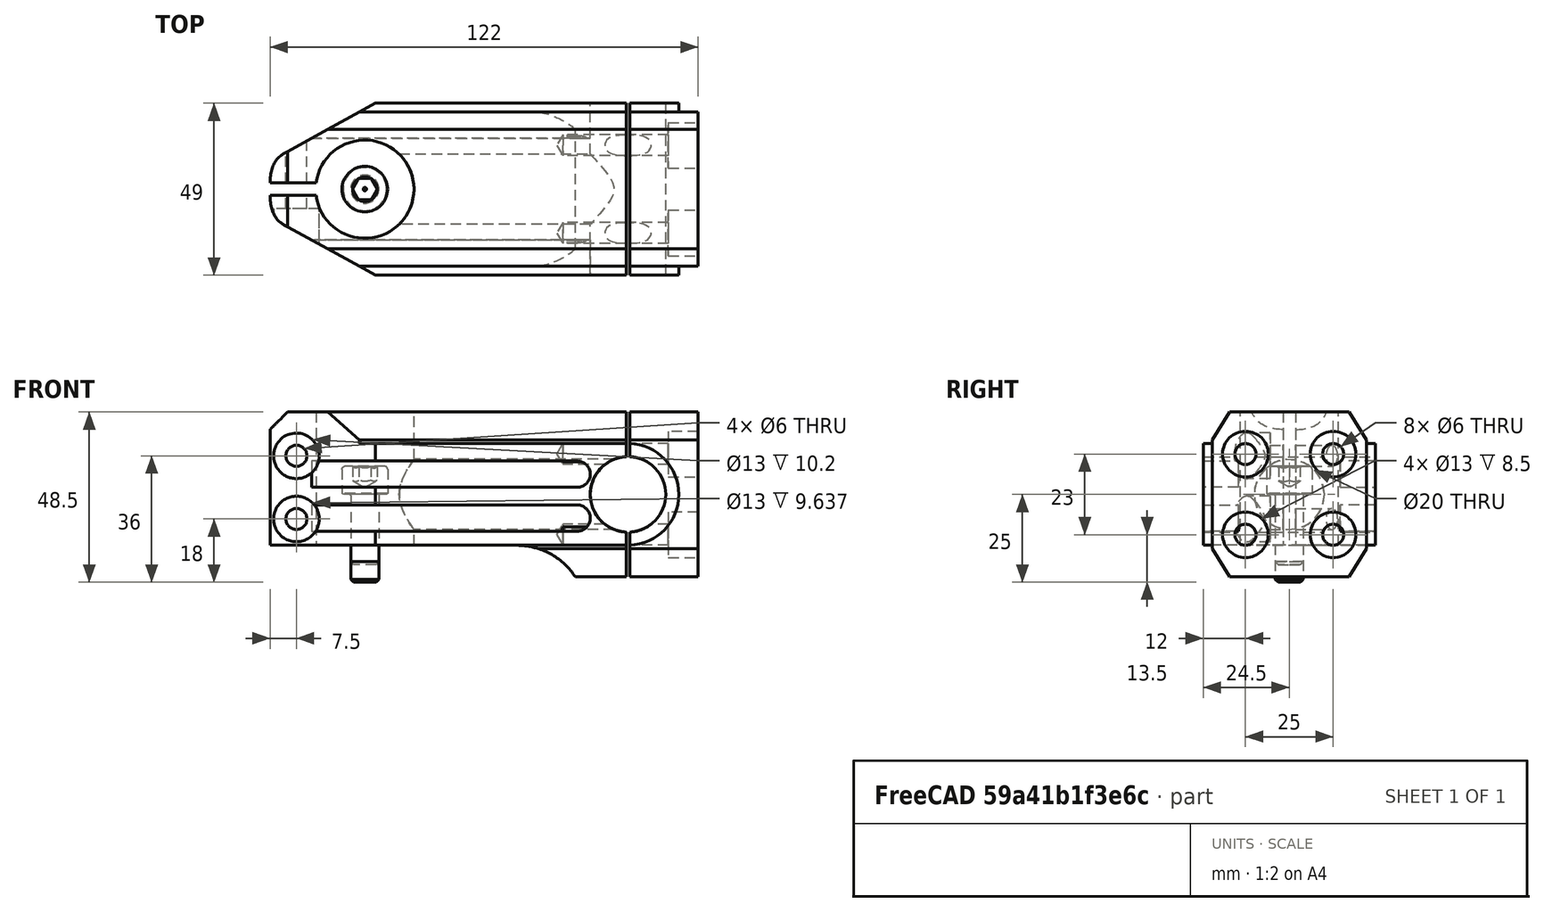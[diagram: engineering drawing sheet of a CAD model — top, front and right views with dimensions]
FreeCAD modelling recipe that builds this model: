
FCSTD DOCUMENT  (FreeCAD 1.0R39109 (Git))
Label: Anchor
License: All rights reserved
LicenseURL: https://en.wikipedia.org/wiki/All_rights_reserved
objects: Sketcher::SketchObject×11, PartDesign::Pocket×9, App::Link×7, App::FeaturePython×7, PartDesign::Pad×2, PartDesign::Hole×2, Part::FeaturePython×2, App::VarSet×1, PartDesign::Chamfer×1, PartDesign::Mirrored×1, PartDesign::Body×1, App::Part×1, Assembly::JointGroup×1, Assembly::AssemblyObject×1
note: 69 computed .brp shape members not serialized (recipe doc carries the construction recipe); baked Part::Feature solids carry a one-line shape summary decoded from their .brp

FEATURE [Sketcher::SketchObject] Sketch
  ArcFitTolerance = 1e-06
  AttachmentSupport = -> [XZ_Plane001]
  FullyConstrained = true
  MakeInternals = false
  MapMode = 5
  Placement = pos=(0,0,0) rot=(1,0,0;1.5708rad)
  expr: Constraints[15] = <<VarSet>>.Size
  expr: Constraints[16] = <<VarSet>>.Size + 20 mm
  sketch-geometry (7):
    g0: Circle CenterX=75 CenterY=0 CenterZ=0 NormalX=0 NormalY=0 NormalZ=1 AngleXU=0 Radius=10.75
    g1: LineSegment StartX=0 StartY=23.5 StartZ=0 EndX=95 EndY=23.5 EndZ=0
    g2: LineSegment StartX=95 StartY=23.5 StartZ=0 EndX=95 EndY=-23.5 EndZ=0
    g3: LineSegment StartX=95 StartY=-23.5 StartZ=0 EndX=0 EndY=-23.5 EndZ=0
    g4: LineSegment StartX=0 StartY=-23.5 StartZ=0 EndX=-27 EndY=-23.5 EndZ=0
    g5: LineSegment StartX=-27 StartY=-23.5 StartZ=0 EndX=-27 EndY=23.5 EndZ=0
    g6: LineSegment StartX=-27 StartY=23.5 StartZ=0 EndX=0 EndY=23.5 EndZ=0
  constraints (20):
    c: Diameter(g0) = 21.5
    c: PointOnObject(g0,g-1)
    c: PointOnObject(g1,g-2)
    c: Horizontal(g1)
    c: Coincident(g1,g2)
    c: Coincident(g2,g3)
    c: PointOnObject(g3,g-2)
    c: Horizontal(g3)
    c: Coincident(g3,g4)
    c: Horizontal(g4)
    c: Coincident(g4,g5)
    c: Vertical(g5)
    c: Coincident(g5,g6)
    c: Coincident(g6,g1)
    c: Parallel(g6,g-1)
    c: Distance(g0,g-1) = 75
    c: Distance(g1) = 95
    c: Distance(g2) = 47
    c: Distance(g4) = 27
    c: Symmetric(g1,g2,g-1)
FEATURE [App::VarSet] VarSet
  Size = 75
FEATURE [PartDesign::Pad] Pad
  Direction = (0,-1,2e-16)
  Length = 22
  Length2 = 10
  Placement = pos=(0,0,0) rot=(1,0,0;1.5708rad)
  Profile = -> Sketch
  ReferenceAxis = -> Sketch [N_Axis]
  Refine = true
  Suppressed = false
  Type = 0
FEATURE [PartDesign::Chamfer] Chamfer
  Angle = 45
  Base = -> Pad [Edge14,Edge15]
  BaseFeature = -> Pad
  ChamferType = 1
  FlipDirection = false
  Placement = pos=(0,0,0) rot=(1,0,0;1.5708rad)
  Refine = true
  Size = 8
  Size2 = 5
  SupportTransform = false
  Suppressed = false
  UseAllEdges = false
FEATURE [Sketcher::SketchObject] Sketch001
  ArcFitTolerance = 1e-06
  AttachmentSupport = -> [Chamfer]
  ExternalGeometry = -> [Chamfer]
  FullyConstrained = true
  MakeInternals = false
  MapMode = 5
  Placement = pos=(0,-22,0) rot=(1,0,0;1.5708rad)
  sketch-geometry (5):
    g0: ArcOfCircle CenterX=75 CenterY=4.9e-15 CenterZ=0 NormalX=0 NormalY=0 NormalZ=1 AngleXU=0 Radius=14.5 StartAngle=4.71239 EndAngle=7.85398
    g1: LineSegment StartX=75 StartY=14.5 StartZ=0 EndX=-27 EndY=14.5 EndZ=0
    g2: LineSegment StartX=75 StartY=-14.5 StartZ=0 EndX=-27 EndY=-14.5 EndZ=0
    g3: LineSegment StartX=-27 StartY=14.5 StartZ=0 EndX=-27 EndY=-14.5 EndZ=0
    g4: Circle CenterX=75 CenterY=4.9e-15 CenterZ=0 NormalX=0 NormalY=0 NormalZ=1 AngleXU=0 Radius=10.75
  constraints (14):
    c: Coincident(g0,g-4)
    c: Vertical(g0,g0)
    c: Vertical(g0,g0)
    c: Coincident(g0,g1)
    c: Coincident(g0,g2)
    c: Horizontal(g1)
    c: Horizontal(g2)
    c: Radius(g0) = 14.5
    c: Vertical(g3)
    c: Coincident(g1,g3)
    c: Coincident(g2,g3)
    c: Distance(g-1,g3) = 27
    c: Coincident(g4,g0)
    c: Equal(g4,g-4)
FEATURE [PartDesign::Pad] Pad001
  BaseFeature = -> Chamfer
  Direction = (0,-1,2e-16)
  Length = 2.5
  Length2 = 10
  Placement = pos=(0,0,0) rot=(1,0,0;1.5708rad)
  Profile = -> Sketch001
  ReferenceAxis = -> Sketch001 [N_Axis]
  Refine = true
  Suppressed = false
  Type = 0
FEATURE [Sketcher::SketchObject] Sketch002
  ArcFitTolerance = 1e-06
  AttachmentSupport = -> [Pad001]
  ExternalGeometry = -> [Pad001]
  FullyConstrained = true
  MakeInternals = false
  MapMode = 5
  Placement = pos=(0,-24.5,6.1e-15) rot=(1,0,0;1.5708rad)
  expr: Constraints[18] = VarSet.Size - 14.5 mm
  sketch-geometry (8):
    g0: LineSegment StartX=-27 StartY=9.5 StartZ=0 EndX=-27 EndY=2 EndZ=0
    g1: LineSegment StartX=-27 StartY=2 StartZ=0 EndX=60.5 EndY=2 EndZ=0
    g2: LineSegment StartX=60.5 StartY=9.5 StartZ=0 EndX=-27 EndY=9.5 EndZ=0
    g3: LineSegment StartX=-27 StartY=-3 StartZ=0 EndX=-27 EndY=-10.5 EndZ=0
    g4: LineSegment StartX=-27 StartY=-10.5 StartZ=0 EndX=60.5 EndY=-10.5 EndZ=0
    g5: LineSegment StartX=60.5 StartY=-3 StartZ=0 EndX=-27 EndY=-3 EndZ=0
    g6: ArcOfCircle CenterX=60.5 CenterY=5.75 CenterZ=0 NormalX=0 NormalY=0 NormalZ=1 AngleXU=0 Radius=3.75 StartAngle=4.71239 EndAngle=7.85398
    g7: ArcOfCircle CenterX=60.5 CenterY=-6.75 CenterZ=0 NormalX=0 NormalY=0 NormalZ=1 AngleXU=0 Radius=3.75 StartAngle=4.71239 EndAngle=7.85398
  constraints (22):
    c: Coincident(g0,g1)
    c: Coincident(g2,g0)
    c: Vertical(g0)
    c: Horizontal(g1)
    c: Horizontal(g2)
    c: PointOnObject(g0,g-3)
    c: Coincident(g3,g4)
    c: Coincident(g5,g3)
    c: Vertical(g3)
    c: Horizontal(g4)
    c: Horizontal(g5)
    c: PointOnObject(g3,g-3)
    c: Tangent(g6,g2) = -1.5708
    c: Tangent(g6,g1) = -1.5708
    c: Tangent(g7,g5) = -1.5708
    c: Tangent(g7,g4) = -1.5708
    c: Distance(g1,g2) = 7.5
    c: Distance(g-1,g1) = 2
    c: Distance(g6,g-2) = 60.5
    c: Vertical(g6,g7)
    c: Equal(g3,g0)
    c: Distance(g-1,g5) = 3
FEATURE [PartDesign::Pocket] Pocket
  BaseFeature = -> Pad001
  Direction = (0,1,-2e-16)
  Length = 10
  Length2 = 5
  Placement = pos=(0,0,0) rot=(1,0,0;1.5708rad)
  Profile = -> Sketch002
  ReferenceAxis = -> Sketch002 [N_Axis]
  Refine = true
  Suppressed = false
  Type = 0
FEATURE [Sketcher::SketchObject] Sketch003
  ArcFitTolerance = 1e-06
  AttachmentSupport = -> [Pocket]
  ExternalGeometry = -> [Pocket]
  FullyConstrained = true
  MakeInternals = false
  MapMode = 5
  Placement = pos=(0,-22,0) rot=(1,0,0;1.5708rad)
  expr: Constraints[9] = VarSet.Size - 15 mm
  sketch-geometry (5):
    g0: LineSegment StartX=43.2967 StartY=-14.5 StartZ=0 EndX=-27 EndY=-14.5 EndZ=0
    g1: LineSegment StartX=-27 StartY=-14.5 StartZ=0 EndX=-27 EndY=-23.5 EndZ=0
    g2: LineSegment StartX=-27 StartY=-23.5 StartZ=0 EndX=0 EndY=-23.5 EndZ=0
    g3: LineSegment StartX=0 StartY=-23.5 StartZ=0 EndX=60 EndY=-23.5 EndZ=0
    g4: ArcOfCircle CenterX=43.2967 CenterY=-34.5 CenterZ=0 NormalX=0 NormalY=0 NormalZ=1 AngleXU=0 Radius=20 StartAngle=0.582364 EndAngle=1.5708
  constraints (13):
    c: PointOnObject(g0,g-5)
    c: Coincident(g0,g-5)
    c: Coincident(g0,g1)
    c: Coincident(g1,g-4)
    c: Coincident(g1,g2)
    c: PointOnObject(g2,g-3)
    c: Coincident(g2,g3)
    c: PointOnObject(g3,g-3)
    c: PointOnObject(g2,g-2)
    c: DistanceX(g3,g3) = 60
    c: Coincident(g3,g4)
    c: Tangent(g4,g0) = -1.5708
    c: Radius(g4) = 20
FEATURE [PartDesign::Pocket] Pocket001
  BaseFeature = -> Pocket
  Direction = (0,1,-2e-16)
  Length = 5
  Length2 = 5
  Placement = pos=(0,0,0) rot=(1,0,0;1.5708rad)
  Profile = -> Sketch003
  ReferenceAxis = -> Sketch003 [N_Axis]
  Refine = true
  Suppressed = false
  Type = 1
FEATURE [Sketcher::SketchObject] Sketch004
  ArcFitTolerance = 1e-06
  AttachmentSupport = -> [Pocket001]
  ExternalGeometry = -> [Pocket001]
  FullyConstrained = true
  MakeInternals = false
  MapMode = 5
  Placement = pos=(0,1.13e-14,23.5) rot=(0,0,1;3.14159rad)
  sketch-geometry (10):
    g0: LineSegment StartX=-3 StartY=24.5 StartZ=0 EndX=27 EndY=24.5 EndZ=0
    g1: LineSegment StartX=27 StartY=24.5 StartZ=0 EndX=27 EndY=1.75 EndZ=0
    g2: LineSegment StartX=-3 StartY=24.5 StartZ=0 EndX=23 EndY=10.2 EndZ=0
    g3: LineSegment [constr] StartX=23 StartY=10.2 StartZ=0 EndX=27 EndY=8 EndZ=0
    g4: Circle [constr] CenterX=23 CenterY=10.2 CenterZ=0 NormalX=0 NormalY=0 NormalZ=1 AngleXU=0 Radius=1
    g5: Circle [constr] CenterX=27 CenterY=8 CenterZ=0 NormalX=0 NormalY=0 NormalZ=1 AngleXU=0 Radius=1
    g6: Circle [constr] CenterX=27 CenterY=1.75 CenterZ=0 NormalX=0 NormalY=0 NormalZ=1 AngleXU=0 Radius=1
    g7: BSplineCurve PolesCount=3 KnotsCount=2 Degree=2 IsPeriodic=0
    g8: GeomPoint [constr] X=23 Y=10.2 Z=0
    g9: GeomPoint [constr] X=27 Y=1.75 Z=0
  constraints (23):
    c: PointOnObject(g0,g-3)
    c: Coincident(g0,g-4)
    c: Coincident(g0,g1)
    c: PointOnObject(g1,g-6)
    c: DistanceY(g-6,g1) = 1.75
    c: Distance(g0,g-2) = 3
    c: Coincident(g0,g2)
    c: Distance(g2,g-2) = 23
    c: Coincident(g3,g2)
    c: PointOnObject(g3,g1)
    c: Parallel(g3,g2)
    c: DistanceY(g-6,g3) = 8
    c: Weight(g4) = 1
    c: Equal(g4,g5)
    c: Equal(g4,g6)
    c: InternalAlignment(g4,g7)
    c: InternalAlignment(g5,g7)
    c: InternalAlignment(g6,g7)
    c: InternalAlignment(g8,g7)
    c: InternalAlignment(g9,g7)
    c: Coincident(g4,g2)
    c: Coincident(g6,g1)
    c: Coincident(g5,g3)
FEATURE [PartDesign::Pocket] Pocket002
  BaseFeature = -> Pocket001
  Direction = (0,0,-1)
  Length = 5
  Length2 = 5
  Placement = pos=(0,0,0) rot=(1,0,0;1.5708rad)
  Profile = -> Sketch004
  ReferenceAxis = -> Sketch004 [N_Axis]
  Refine = true
  Suppressed = false
  Type = 1
FEATURE [PartDesign::Mirrored] Mirrored
  BaseFeature = -> Pocket002
  MirrorPlane = -> XZ_Plane001
  Placement = pos=(0,0,0) rot=(1,0,0;1.5708rad)
  Refine = true
  Suppressed = false
  TransformMode = 1
FEATURE [Sketcher::SketchObject] Sketch005
  ArcFitTolerance = 1e-06
  AttachmentSupport = -> [Mirrored]
  ExternalGeometry = -> [Mirrored]
  FullyConstrained = true
  MakeInternals = false
  MapMode = 5
  Placement = pos=(0,0,23.5) rot=(0,0,1;3.14159rad)
  sketch-geometry (4):
    g0: ArcOfCircle CenterX=0 CenterY=0 CenterZ=0 NormalX=0 NormalY=0 NormalZ=1 AngleXU=0 Radius=14 StartAngle=0.125328 EndAngle=6.15786
    g1: LineSegment StartX=27 StartY=1.75 StartZ=0 EndX=13.8902 EndY=1.75 EndZ=0
    g2: LineSegment StartX=27 StartY=-1.75 StartZ=0 EndX=13.8902 EndY=-1.75 EndZ=0
    g3: LineSegment StartX=27 StartY=1.75 StartZ=0 EndX=27 EndY=-1.75 EndZ=0
  constraints (10):
    c: Diameter(g0) = 28
    c: Coincident(g0,g-1)
    c: Coincident(g1,g-3)
    c: Horizontal(g1)
    c: Coincident(g2,g-3)
    c: Horizontal(g2)
    c: Coincident(g3,g1)
    c: Coincident(g3,g2)
    c: Coincident(g0,g2)
    c: Coincident(g0,g1)
FEATURE [PartDesign::Pocket] Pocket003
  BaseFeature = -> Mirrored
  Direction = (0,0,-1)
  Length = 5
  Length2 = 5
  Placement = pos=(0,0,0) rot=(1,0,0;1.5708rad)
  Profile = -> Sketch005
  ReferenceAxis = -> Sketch005 [N_Axis]
  Refine = true
  Suppressed = false
  Type = 1
FEATURE [Sketcher::SketchObject] Sketch006
  ArcFitTolerance = 1e-06
  AttachmentSupport = -> [XZ_Plane001]
  ExternalGeometry = -> [Pocket003]
  FullyConstrained = true
  MakeInternals = false
  MapMode = 5
  Placement = pos=(0,0,0) rot=(1,0,0;1.5708rad)
  sketch-geometry (3):
    g0: LineSegment StartX=-27 StartY=23.5 StartZ=0 EndX=-22 EndY=23.5 EndZ=0
    g1: LineSegment StartX=-22 StartY=23.5 StartZ=0 EndX=-27 EndY=18.5 EndZ=0
    g2: LineSegment StartX=-27 StartY=18.5 StartZ=0 EndX=-27 EndY=23.5 EndZ=0
  constraints (8):
    c: Coincident(g0,g-4)
    c: PointOnObject(g0,g-5)
    c: Coincident(g0,g1)
    c: PointOnObject(g1,g-3)
    c: Coincident(g1,g2)
    c: Coincident(g2,g0)
    c: DistanceX(g0,g0) = 5
    c: DistanceY(g2,g2) = 5
FEATURE [PartDesign::Pocket] Pocket004
  BaseFeature = -> Pocket003
  Direction = (0,1,-2e-16)
  Length = 5
  Length2 = 5
  Midplane = true
  Placement = pos=(0,0,0) rot=(1,0,0;1.5708rad)
  Profile = -> Sketch006
  ReferenceAxis = -> Sketch006 [N_Axis]
  Refine = true
  Suppressed = false
  Type = 1
FEATURE [Sketcher::SketchObject] Sketch007
  ArcFitTolerance = 1e-06
  AttachmentSupport = -> [Pocket004]
  FullyConstrained = true
  MakeInternals = false
  MapMode = 5
  Placement = pos=(95,0,0) rot=(0.707107,0,0.707107;3.14159rad)
  sketch-geometry (4):
    g0: Circle CenterX=11.5 CenterY=12.5 CenterZ=0 NormalX=0 NormalY=0 NormalZ=1 AngleXU=0 Radius=6.5
    g1: Circle CenterX=-11.5 CenterY=12.5 CenterZ=0 NormalX=0 NormalY=0 NormalZ=1 AngleXU=0 Radius=6.5
    g2: Circle CenterX=-11.5 CenterY=-12.5 CenterZ=0 NormalX=0 NormalY=0 NormalZ=1 AngleXU=0 Radius=6.5
    g3: Circle CenterX=11.5 CenterY=-12.5 CenterZ=0 NormalX=0 NormalY=0 NormalZ=1 AngleXU=0 Radius=6.5
  constraints (9):
    c: Symmetric(g0,g3,g-1)
    c: Symmetric(g1,g2,g-1)
    c: Symmetric(g2,g3,g-2)
    c: DistanceX(g1,g0) = 23
    c: DistanceY(g3,g0) = 25
    c: Equal(g0,g1)
    c: Equal(g1,g2)
    c: Equal(g2,g3)
    c: Diameter(g0) = 13
FEATURE [PartDesign::Pocket] Pocket005
  BaseFeature = -> Pocket004
  Direction = (-1,0,2e-16)
  Length = 8.5
  Length2 = 5
  Placement = pos=(0,0,0) rot=(1,0,0;1.5708rad)
  Profile = -> Sketch007
  ReferenceAxis = -> Sketch007 [N_Axis]
  Refine = true
  Suppressed = false
  Type = 0
FEATURE [PartDesign::Hole] Hole
  BaseFeature = -> Pocket005
  CustomThreadClearance = 0
  Depth = 30
  DepthType = 0
  Diameter = 6
  DrillForDepth = false
  DrillPoint = 1
  DrillPointAngle = 118
  HoleCutCountersinkAngle = 90
  HoleCutCustomValues = false
  HoleCutDepth = 0
  HoleCutDiameter = 6.1
  HoleCutType = 0
  ModelThread = false
  Placement = pos=(0,0,0) rot=(1,0,0;1.5708rad)
  Profile = -> Pocket005 [Face49,Face47,Face46,Face48]
  Refine = true
  Suppressed = false
  Tapered = false
  TaperedAngle = 90
  ThreadClass = 0
  ThreadDepth = 30
  ThreadDepthType = 0
  ThreadDirection = 0
  ThreadFit = 0
  ThreadSize = 0
  ThreadType = 0
  Threaded = false
  UseCustomThreadClearance = false
FEATURE [Sketcher::SketchObject] Sketch008
  ArcFitTolerance = 1e-06
  AttachmentSupport = -> [Hole]
  FullyConstrained = true
  MakeInternals = false
  MapMode = 5
  Placement = pos=(0,-14.5,4.8e-15) rot=(1,0,0;1.5708rad)
  sketch-geometry (2):
    g0: Circle CenterX=-19.5 CenterY=11 CenterZ=0 NormalX=0 NormalY=0 NormalZ=1 AngleXU=0 Radius=6.5
    g1: Circle CenterX=-19.5 CenterY=-7 CenterZ=0 NormalX=0 NormalY=0 NormalZ=1 AngleXU=0 Radius=6.5
  constraints (6):
    c: Vertical(g0,g1)
    c: Equal(g1,g0)
    c: DistanceY(g1,g-1) = 7
    c: Distance(g0,g-1) = 11
    c: DistanceX(g0,g-1) = 19.5
    c: Diameter(g0) = 13
FEATURE [PartDesign::Pocket] Pocket006
  BaseFeature = -> Hole
  Direction = (0,1,-2e-16)
  Length = 9
  Length2 = 7
  Placement = pos=(0,0,0) rot=(1,0,0;1.5708rad)
  Profile = -> Sketch008
  ReferenceAxis = -> Sketch008 [N_Axis]
  Refine = true
  Suppressed = false
  Type = 4
FEATURE [PartDesign::Hole] Hole001
  BaseFeature = -> Pocket006
  CustomThreadClearance = 0
  Depth = 25
  DepthType = 0
  Diameter = 6
  DrillForDepth = false
  DrillPoint = 1
  DrillPointAngle = 118
  HoleCutCountersinkAngle = 90
  HoleCutCustomValues = false
  HoleCutDepth = 0
  HoleCutDiameter = 6.1
  HoleCutType = 0
  ModelThread = false
  Placement = pos=(0,0,0) rot=(1,0,0;1.5708rad)
  Profile = -> Pocket006 [Face33,Face57]
  Refine = true
  Suppressed = false
  Tapered = false
  TaperedAngle = 90
  ThreadClass = 0
  ThreadDepth = 25
  ThreadDepthType = 0
  ThreadDirection = 0
  ThreadFit = 0
  ThreadSize = 0
  ThreadType = 0
  Threaded = false
  UseCustomThreadClearance = false
FEATURE [Sketcher::SketchObject] Sketch009
  ArcFitTolerance = 1e-06
  AttachmentSupport = -> [XZ_Plane001]
  ExternalGeometry = -> [Hole001]
  FullyConstrained = true
  MakeInternals = false
  MapMode = 5
  Placement = pos=(0,0,0) rot=(1,0,0;1.5708rad)
  expr: Constraints[10] = VarSet.Size + 0.5 mm
  expr: Constraints[9] = VarSet.Size - 0.5 mm
  sketch-geometry (4):
    g0: LineSegment StartX=74.5 StartY=23.5 StartZ=0 EndX=74.5 EndY=-23.5 EndZ=0
    g1: LineSegment StartX=74.5 StartY=-23.5 StartZ=0 EndX=75.5 EndY=-23.5 EndZ=0
    g2: LineSegment StartX=75.5 StartY=-23.5 StartZ=0 EndX=75.5 EndY=23.5 EndZ=0
    g3: LineSegment StartX=75.5 StartY=23.5 StartZ=0 EndX=74.5 EndY=23.5 EndZ=0
  constraints (12):
    c: Coincident(g0,g1)
    c: Coincident(g1,g2)
    c: Coincident(g2,g3)
    c: Coincident(g3,g0)
    c: Vertical(g0)
    c: Vertical(g2)
    c: Horizontal(g1)
    c: Horizontal(g3)
    c: PointOnObject(g0,g-3)
    c: Distance(g-2,g0) = 74.5
    c: Distance(g-2,g2) = 75.5
    c: PointOnObject(g0,g-4)
FEATURE [PartDesign::Pocket] Pocket007
  BaseFeature = -> Hole001
  Direction = (0,1,-2e-16)
  Length = 5
  Length2 = 5
  Midplane = true
  Placement = pos=(0,0,0) rot=(1,0,0;1.5708rad)
  Profile = -> Sketch009
  ReferenceAxis = -> Sketch009 [N_Axis]
  Refine = true
  Suppressed = false
  Type = 1
FEATURE [Sketcher::SketchObject] Sketch010
  ArcFitTolerance = 1e-06
  AttachmentSupport = -> [YZ_Plane001]
  FullyConstrained = true
  MakeInternals = false
  MapMode = 5
  Placement = pos=(0,0,0) rot=(0.57735,0.57735,0.57735;2.0944rad)
  sketch-geometry (1):
    g0: Circle CenterX=0 CenterY=0 CenterZ=0 NormalX=0 NormalY=0 NormalZ=1 AngleXU=0 Radius=10
  constraints (2):
    c: Diameter(g0) = 20
    c: Coincident(g0,g-1)
FEATURE [PartDesign::Pocket] Pocket008
  BaseFeature = -> Pocket007
  Direction = (-1,0,0)
  Length = 0
  Length2 = 5
  Placement = pos=(0,0,0) rot=(1,0,0;1.5708rad)
  Profile = -> Sketch010
  ReferenceAxis = -> Sketch010 [N_Axis]
  Refine = true
  Suppressed = false
  Type = 3
  UpToFace = -> Pocket007 [Face18]
FEATURE [PartDesign::Body] Body  label="Stem"
  AllowCompound = true
  Group = -> [Sketch,Pad,Chamfer,Sketch001,Pad001,Sketch002,Pocket,Sketch003,Pocket001,Sketch004,Pocket002,Mirrored,Sketch005,Pocket003,Sketch006,Pocket004,Sketch007,Pocket005,Hole,Sketch008,Pocket006,Hole001,Sketch009,Pocket007,Sketch010,Pocket008]
  Origin = -> Origin001
  Tip = -> Pocket008
FEATURE [App::Part] Part
  Group = -> [Body,VarSet]
  Origin = -> Origin
FEATURE [Part::FeaturePython] Screw  label="M8x25-Screw"  # WARN: FeaturePython — macro-defined, semantics opaque (R4)
  Diameter = 8
  Invert = false
  LeftHanded = false
  Length = 5
  LengthCustom = 25
  MatchOuter = false
  OffsetAngle = 0
  Thread = false
  Type = 75
FEATURE [App::Link] Stem  label="Stem001"
  LinkedObject = -> Body
FEATURE [App::FeaturePython] GroundedJoint  # Assembly grounded joint (typed FeaturePython)
  ObjectToGround = -> Stem
FEATURE [App::Link] M8x25_Screw  label="M8x25-Screw001"
  LinkPlacement = pos=(87.5,-12.5,-11.5) rot=(0.707107,0,0.707107;3.14159rad)
  LinkedObject = -> Screw
  Placement = pos=(87.5,-12.5,-11.5) rot=(0.707107,0,0.707107;3.14159rad)
FEATURE [App::FeaturePython] Joint  label="Fixed"  # Assembly joint (typed FeaturePython)
  Activated = true
  AngleMax = 0
  AngleMin = 0
  Detach1 = false
  Detach2 = false
  Distance = 0
  Distance2 = 0
  EnableAngleMax = false
  EnableAngleMin = false
  EnableLengthMax = false
  EnableLengthMin = false
  JointType = 0 (Fixed)
  LengthMax = 0
  LengthMin = 0
  Offset2 = pos=(0,0,1) rot=(0,0,1;0rad)
  Placement2 = pos=(87.5,-12.5,-11.5) rot=(0.707107,0,0.707107;3.14159rad)
  Reference1 = -> Assembly [M8x25_Screw.Edge26,M8x25_Screw.Edge26]
  Reference2 = -> Assembly [Stem.Edge282,Stem.Edge282]
FEATURE [App::Link] M8x25_Screw001  label="M8x25-Screw002"
  LinkPlacement = pos=(87.5,-12.5,11.5) rot=(0.707107,0,0.707107;3.14159rad)
  LinkedObject = -> Screw
  Placement = pos=(87.5,-12.5,11.5) rot=(0.707107,0,0.707107;3.14159rad)
FEATURE [App::Link] M8x25_Screw002  label="M8x25-Screw003"
  LinkPlacement = pos=(87.5,12.5,11.5) rot=(0.707107,0,0.707107;3.14159rad)
  LinkedObject = -> Screw
  Placement = pos=(87.5,12.5,11.5) rot=(0.707107,0,0.707107;3.14159rad)
FEATURE [App::Link] M8x25_Screw003  label="M8x25-Screw004"
  LinkPlacement = pos=(87.5,12.5,-11.5) rot=(0.707107,0,0.707107;3.14159rad)
  LinkedObject = -> Screw
  Placement = pos=(87.5,12.5,-11.5) rot=(0.707107,0,0.707107;3.14159rad)
FEATURE [App::FeaturePython] Joint001  label="Fixed001"  # Assembly joint (typed FeaturePython)
  Activated = true
  AngleMax = 0
  AngleMin = 0
  Detach1 = false
  Detach2 = false
  Distance = 0
  Distance2 = 0
  EnableAngleMax = false
  EnableAngleMin = false
  EnableLengthMax = false
  EnableLengthMin = false
  JointType = 0 (Fixed)
  LengthMax = 0
  LengthMin = 0
  Offset2 = pos=(0,0,1) rot=(0,0,1;0rad)
  Placement2 = pos=(87.5,12.5,-11.5) rot=(0.707107,0,0.707107;3.14159rad)
  Reference1 = -> Assembly [M8x25_Screw003.Edge26,M8x25_Screw003.Edge26]
  Reference2 = -> Assembly [Stem.Edge280,Stem.Edge280]
FEATURE [App::FeaturePython] Joint002  label="Fixed002"  # Assembly joint (typed FeaturePython)
  Activated = true
  AngleMax = 0
  AngleMin = 0
  Detach1 = false
  Detach2 = false
  Distance = 0
  Distance2 = 0
  EnableAngleMax = false
  EnableAngleMin = false
  EnableLengthMax = false
  EnableLengthMin = false
  JointType = 0 (Fixed)
  LengthMax = 0
  LengthMin = 0
  Offset2 = pos=(0,0,1) rot=(0,0,1;0rad)
  Placement2 = pos=(87.5,12.5,11.5) rot=(0.707107,0,0.707107;3.14159rad)
  Reference1 = -> Assembly [M8x25_Screw002.Edge26,M8x25_Screw002.Edge26]
  Reference2 = -> Assembly [Stem.Edge276,Stem.Edge276]
FEATURE [App::FeaturePython] Joint003  label="Fixed003"  # Assembly joint (typed FeaturePython)
  Activated = true
  AngleMax = 0
  AngleMin = 0
  Detach1 = false
  Detach2 = false
  Distance = 0
  Distance2 = 0
  EnableAngleMax = false
  EnableAngleMin = false
  EnableLengthMax = false
  EnableLengthMin = false
  JointType = 0 (Fixed)
  LengthMax = 0
  LengthMin = 0
  Offset2 = pos=(0,0,1) rot=(0,0,1;0rad)
  Placement2 = pos=(87.5,-12.5,11.5) rot=(0.707107,0,0.707107;3.14159rad)
  Reference1 = -> Assembly [M8x25_Screw001.Edge26,M8x25_Screw001.Edge26]
  Reference2 = -> Assembly [Stem.Edge278,Stem.Edge278]
FEATURE [Part::FeaturePython] Screw001  label="M8x20-Screw"  # WARN: FeaturePython — macro-defined, semantics opaque (R4)
  Diameter = 8
  Invert = false
  LeftHanded = false
  Length = 17
  LengthCustom = 20
  MatchOuter = false
  OffsetAngle = 0
  Thread = false
  Type = 75
FEATURE [App::Link] M8x20_Screw  label="M8x20-Screw001"
  LinkPlacement = pos=(-19.5,-5.5,11) rot=(1,0,0;1.5708rad)
  LinkedObject = -> Screw001
  Placement = pos=(-19.5,-5.5,11) rot=(1,0,0;1.5708rad)
FEATURE [App::Link] M8x20_Screw001  label="M8x20-Screw002"
  LinkPlacement = pos=(-19.5,-5.5,-7) rot=(1,0,0;1.5708rad)
  LinkedObject = -> Screw001
  Placement = pos=(-19.5,-5.5,-7) rot=(1,0,0;1.5708rad)
FEATURE [App::FeaturePython] Joint004  label="Fixed004"  # Assembly joint (typed FeaturePython)
  Activated = true
  AngleMax = 0
  AngleMin = 0
  Detach1 = false
  Detach2 = false
  Distance = 0
  Distance2 = 0
  EnableAngleMax = false
  EnableAngleMin = false
  EnableLengthMax = false
  EnableLengthMin = false
  JointType = 0 (Fixed)
  LengthMax = 0
  LengthMin = 0
  Placement2 = pos=(-19.5,-5.5,-7) rot=(1,0,0;1.5708rad)
  Reference1 = -> Assembly [M8x20_Screw001.Edge26,M8x20_Screw001.Edge26]
  Reference2 = -> Assembly [Stem.Edge142,Stem.Edge142]
FEATURE [App::FeaturePython] Joint005  label="Fixed005"  # Assembly joint (typed FeaturePython)
  Activated = true
  AngleMax = 0
  AngleMin = 0
  Detach1 = false
  Detach2 = false
  Distance = 0
  Distance2 = 0
  EnableAngleMax = false
  EnableAngleMin = false
  EnableLengthMax = false
  EnableLengthMin = false
  JointType = 0 (Fixed)
  LengthMax = 0
  LengthMin = 0
  Placement2 = pos=(-19.5,-5.5,11) rot=(1,0,0;1.5708rad)
  Reference1 = -> Assembly [M8x20_Screw.Edge26,M8x20_Screw.Edge26]
  Reference2 = -> Assembly [Stem.Edge49,Stem.Edge49]
FEATURE [Assembly::JointGroup] Joints
  Group = -> [GroundedJoint,Joint,Joint001,Joint002,Joint003,Joint004,Joint005]
FEATURE [Assembly::AssemblyObject] Assembly
  Group = -> [Joints,Stem,GroundedJoint,M8x25_Screw,Joint,M8x25_Screw001,M8x25_Screw002,M8x25_Screw003,Joint001,Joint002,Joint003,M8x20_Screw,M8x20_Screw001,Joint004,Joint005]
  Origin = -> Origin002
  Type = Assembly
